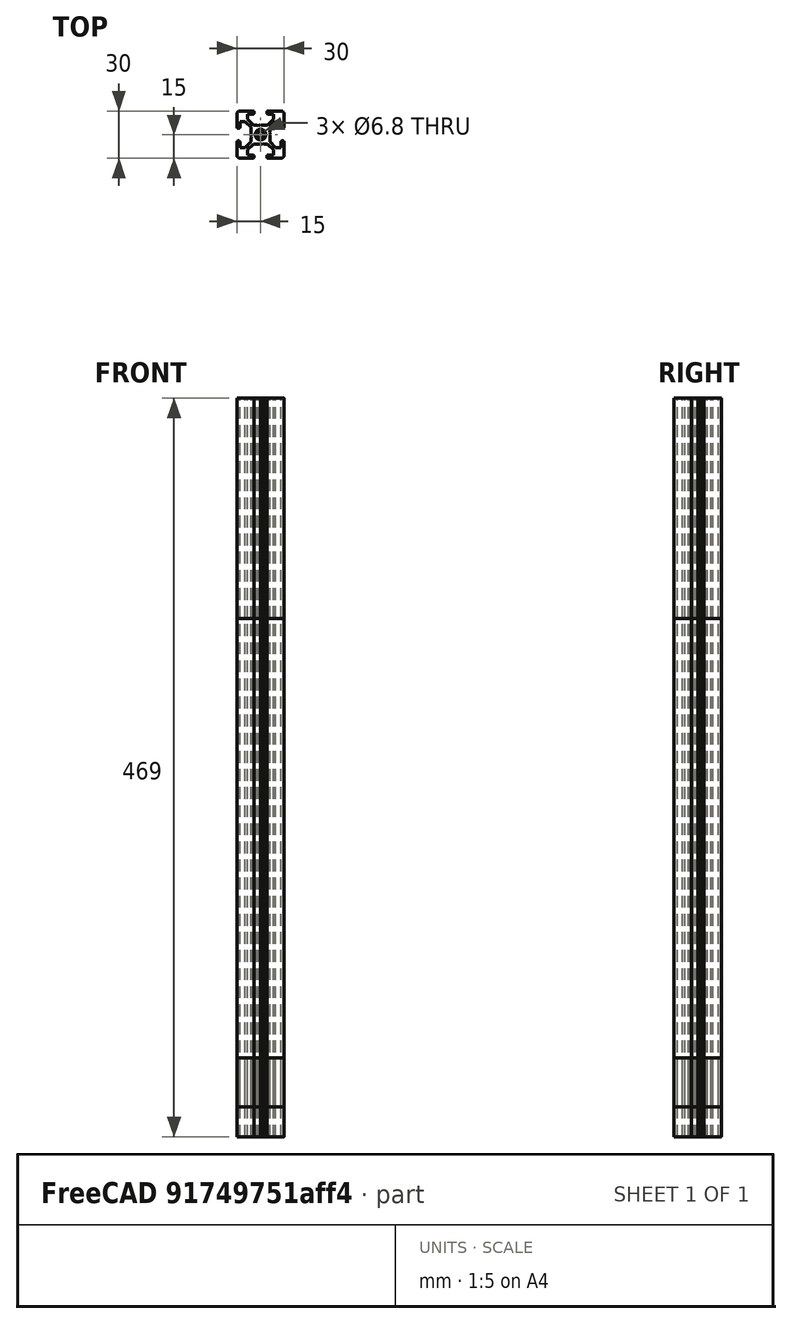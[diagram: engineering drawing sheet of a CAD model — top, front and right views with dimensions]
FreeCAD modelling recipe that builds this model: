
FCSTD DOCUMENT  (FreeCAD 0.18R16146 (Git))
Label: 3030-tslot
License: Other
LicenseURL: GPL3
objects: Part::Feature×6, Part::Extrusion×2, Part::Cylinder×1
note: 9 computed .brp shape members not serialized (recipe doc carries the construction recipe); baked Part::Feature solids carry a one-line shape summary decoded from their .brp

FEATURE [Part::Feature] Part__Feature  label="_GNFS6-3030-50"
  Placement = pos=(0,0,31) rot=(0,0,1;0rad)
  shape: bbox 30 x 30 x 50 mm, 95 faces (baked)
FEATURE [Part::Cylinder] Cylinder
  Angle = 360
  AttacherType = Attacher::AttachEngine3D
  Height = 10
  Radius = 2
FEATURE [Part::Feature] Part__Feature_cs  label="profile-template"
  Placement = pos=(0,0,-1) rot=(0,0,1;0rad)
  shape: bbox 30 x 30 x 3e-07 mm, 0 faces, 0 solids (baked)
FEATURE [Part::Feature] Part__Feature_cs001  label="profile-template001"
  Placement = pos=(0,0,-1) rot=(0,0,1;0rad)
  shape: bbox 30 x 30 x 3e-07 mm, 0 faces, 0 solids (baked)
FEATURE [Part::Extrusion] Extrude  label="310"
  Base = -> Part__Feature_cs001
  Dir = (0,0,1)
  DirMode = 2
  FaceMakerClass = Part::FaceMakerBullseye
  LengthFwd = 310
  LengthRev = 0
  Solid = true
  Symmetric = false
FEATURE [Part::Feature] Extrude001  label="3030-310mm"
  shape: bbox 30 x 30 x 310 mm, 95 faces (baked)
FEATURE [Part::Feature] Part__Feature_cs002  label="profile-template002"
  Placement = pos=(0,0,-1) rot=(0,0,1;0rad)
  shape: bbox 30 x 30 x 3e-07 mm, 0 faces, 0 solids (baked)
FEATURE [Part::Extrusion] Extrude002  label="450"
  Base = -> Part__Feature_cs002
  Dir = (0,0,1)
  DirMode = 2
  FaceMakerClass = Part::FaceMakerBullseye
  LengthFwd = 450
  LengthRev = 0
  Solid = true
  Symmetric = false
FEATURE [Part::Feature] Extrude002001  label="3030-450mm001"
  shape: bbox 30 x 30 x 450 mm, 95 faces (baked)
